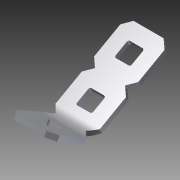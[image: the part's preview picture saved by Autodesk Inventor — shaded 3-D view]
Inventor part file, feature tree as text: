
AUTODESK INVENTOR PART (.ipt)
format: ipt  version: 2014 SP1 (Build 180222100, 222)  size: 546,816 bytes
history: native  units: in
note: dims shown in document units (in); Inventor stores cm internally (conversion verified against a paired STEP export)
features: other x2, sketch x2, imported_body x1, extrude x1
ambient origin geometry x8: Origin, YZ Plane, XZ Plane, XY Plane, X Axis, Y Axis, Z Axis, Center Point
bodies: Body1 (feature_tree)
feature tree (6):
  parser-record x1  (decoder bookkeeping rows leaked as tree rows — omitted from the tree; the rows remain in map.json)
  imported_body  "Base1"
  extrude  "Extrusion1"  Depth=1.0in TaperAngle=0.0deg
  other  "Bend Part1"
  sketch  "Sketch1"  dims[d0=1.5in d1=1.0in d2=0.0in]
  sketch  "Sketch2"  dims[d3=0.5in d4=0.4029in d5=0.2in]
